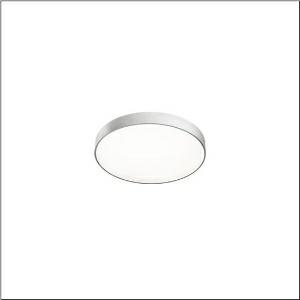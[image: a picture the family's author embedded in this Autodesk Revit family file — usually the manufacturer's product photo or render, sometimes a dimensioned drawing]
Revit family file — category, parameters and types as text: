
# Revit family: round_21_s_51mr34gd0321s
name_source: partatom
category: Lighting Fixtures
units: mm (PartAtom-declared; Revit-internal decimal feet)

## family parameters
Cut with Voids When Loaded = No
Host = Face
Light Source = No
Part Type = Normal
Room Calculation Point = No
Round Connector Dimension = Use Diameter
Shared = No

## types (1)
- Round 21 S (1 x LED, 3930 lm, 28.3 W, 3000K)
    Apparent Load = 28 VA
    CIE Flux Codes = 49 80 96 79 100
    Color Rendering = 80
    Color Temperature = 3000K
    Default Elevation = 1800 mm
    Description = Round 21 S, wall and ceiling luminaire, primary optical cover: cover, of PMMA, opal, light emission: direct/indirect distribution, primary light characteristic: symmetric, installation type: suspended mounting, surface-mounted, LED, rated luminous flux: 3.930lm, luminous efficacy: 139lm/W, light colour: 830, colour temperature: 3000K, control gear: DALI 2, with terminal, 5-pole, mains connection: 230V, AC, 50/60Hz, rated input power: 28.3W, housing, of aluminium, coated, silver, diameter: 400mm, height: 62mm, protection rating (complete): IP40, insulation class (complete): insulation class I (protective earthing), certification: CE, impact resistance: IK04, permissible operating ambient temperature: -10..+35°C, packaging unit: 1 piece
    Height = 87 mm
    Lamp = 1 x LED
    Lamp Light Flux = 3930 lm
    Lamp Power = 28.3 W
    Lamp count = 1
    Length = 400 mm
    Luminous efficacy = 139 lm/W
    Manufacturer = Siteco
    ModVariant = No
    Model = 51MR34GD0321S
    Mounting Place = Ceiling
    Mounting Type = Surface mounted
    Number of Poles = 1
    OnlyDefault = Yes
    Power Factor = 1
    Product Name = Round 21 S
    Product group = wall and ceiling luminaire | ceiling mounted
    ProductGroupID = 304
    Protection Class = Protection class I
    Protection Degree = IP 40
    RLX_Detail_Level = 1
    RLX_Emergency_Light_Flux = 0 lm
    RLX_Emergency_Type = 0
    RLX_Emergency_Type_DB = No
    RlxData = <blob elided: 11581 chars, md5=248c06de>
    Socket = socket
    Standby Power = 0 W
    System Light Flux = 3930 lm
    System Power = 28 W
    Type Comments = Product without accessories
    Type Image = l_1258309.jpg
    URL = http://relux.com
    VarID = ---
    Voltage = 0 V
    Weight = 0.00 kg
    Width = 0 mm  [stored 0 ft]

note: [stored X ft] marks values corroborated as IEEE doubles in the binary element streams (Revit-internal decimal feet)

## geometry (parser evidence)
native form markers: Sweep x13
no freeform markers — native parametric forms only
